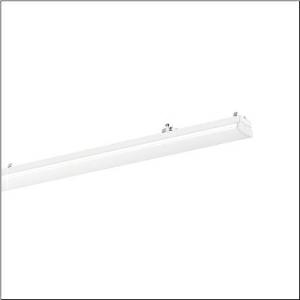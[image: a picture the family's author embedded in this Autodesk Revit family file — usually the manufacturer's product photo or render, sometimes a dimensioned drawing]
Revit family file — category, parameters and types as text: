
# Revit family: licross_21_recessed_opal_ho_52tl1ddn4e5m
name_source: partatom
category: Lighting Fixtures
units: mm (PartAtom-declared; Revit-internal decimal feet)

## family parameters
Cut with Voids When Loaded = No
Host = Face
Light Source = No
Part Type = Normal
Room Calculation Point = No
Round Connector Dimension = Use Diameter
Shared = No

## types (1)
- --- (1 x LED, 14560 lm, 84.6 W, 4000K)
    Apparent Load = 85 VA
    CIE Flux Codes = 44 73 91 87 100
    Color Rendering = 80
    Color Temperature = 4000K
    Default Elevation = 1800 mm
    Description = Licross 21 recessed opal HO, luminaire insert, of sheet steel, galvanised, coil coated, white, length: 1.500mm, width: 66mm, height: 67mm, LED rated luminous flux: 14.560lm, light colour: 840, SDCM (Standard Deviation of Colour Matching)MacAdam ≤ 3 SDCM (initial), control gear: DALI 2, with plug, 5-pole, with phase selection, mains connection: 220..240V, AC, 50/60Hz, rated input power: 85W, internal wiring halogen-free, primary optical cover: cover, of PMMA, light emission: direct with ceiling illumination distribution, primary light characteristic: symmetric, protection rating (complete): IP40, insulation class (complete): insulation class I (protective earthing), certification: CE, ENEC, VDE, UKCA, protection symbol: D if used in an environment without relevant dust loads with corresponding accessories, impact resistance: IK06, permissible ambient temperature for indoor applications: -25..+30°C, corresponds to IFS (International Featured Standards) requirements for safety and quality in the food industry, reducing of maximum allowable ambient temperature of 5°C with ceiling mounting, LABS conformity tested according to VDMA 24364:2018-05, The light source and the operating device comply with the requirements of the Ecodesign Regulation (EU) 2019/2020 and are replaceable in accordance with this regulation, packaging unit: 1 piece
    Height = 83 mm
    Lamp = 1 x LED
    Lamp Light Flux = 14560 lm
    Lamp Power = 84.6 W
    Lamp count = 1
    Length = 1500 mm
    Luminous efficacy = 172 lm/W
    Manufacturer = Siteco
    ModVariant = No
    Model = 52TL1DDN4E5M
    Mounting Place = Ceiling
    Mounting Type = Pendant
    Number of Poles = 1
    OnlyDefault = Yes
    Power Factor = 1
    Product Name = Licross 21 recessed opal HO
    Product group = luminaire insert | ceiling pendant
    ProductGroupID = 901
    Protection Class = Protection class I
    Protection Degree = IP 40
    RLX_Detail_Level = 1
    RLX_Emergency_Light_Flux = 0 lm
    RLX_Emergency_Type = 0
    RLX_Emergency_Type_DB = No
    RlxData = <blob elided: 27401 chars, md5=d1f22611>
    Socket = socket
    Standby Power = 0 W
    System Light Flux = 14560 lm
    System Power = 85 W
    Type Comments = factory setting: luminous flux: 100 % | dim-lin: 254 | 484 mA
    Type Image = l_1313666.jpg
    URL = http://relux.com
    VarID = @adj_076287
    Voltage = 0 V
    Weight = 0.00 kg
    Width = 76 mm

## geometry (parser evidence)
native form markers: Blend x4, Sweep x14
no freeform markers — native parametric forms only
